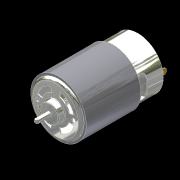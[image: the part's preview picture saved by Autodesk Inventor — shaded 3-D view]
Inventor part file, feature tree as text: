
AUTODESK INVENTOR PART (.ipt)
format: ipt  version: 2012 (Build 160160000, 160)  size: 304,640 bytes
history: native  units: mm (DEFAULTED — no unit token found)
features: sketch x15, extrude x13, fillet x3, plane x3, hole x2, mirror x2, pattern_circular x2, shell x1, chamfer x1
ambient origin geometry x8: Origin, YZ Plane, XZ Plane, XY Plane, X Axis, Y Axis, Z Axis, Center Point
bodies: Solid1 (feature_tree)
feature tree (42):
  extrude  "Extrusion1"  Depth=57.0mm TaperAngle=0.0deg
  fillet  "Fillet1"  Radius=2.0mm
  shell  "Shell1"  Thickness=0.62mm
  extrude  "Extrusion2"  Depth=4.5mm TaperAngle=0.0deg
  fillet  "Fillet2"  Radius=0.5mm
  extrude  "Extrusion3"  Depth=10.0mm TaperAngle=0.0deg
  fillet  "Fillet3"  Radius=1.6mm
  hole  "Hole1"  [1 undecoded]
  mirror  "Mirror1"
  extrude  "Extrusion4"  Depth=13.0mm
  pattern_circular  "Circular Pattern1"  Count=4 Angle=360.0deg
  plane  "Work Plane1"
  extrude  "Extrusion5"  Depth=0.62mm TaperAngle=0.0deg
  extrude  "Extrusion6"  Depth=0.62mm TaperAngle=0.0deg
  extrude  "Extrusion7"  Depth=3.0mm TaperAngle=0.0deg
  extrude  "Extrusion8"  Depth=0.8mm TaperAngle=0.0deg
  extrude  "Extrusion9"  Depth=1.0mm TaperAngle=0.0deg
  extrude  "Extrusion10"  Depth=3.15mm
  pattern_circular  "Circular Pattern2"  [2 undecoded]
  extrude  "Extrusion11"  Depth=1.0mm TaperAngle=0.0deg
  chamfer  "Chamfer1"  Distance=40.0mm Angle=360.0deg
  hole  "Hole2"  [1 undecoded]
  mirror  "Mirror2"
  plane  "Work Plane2"
  extrude  "Extrusion12"  Depth=3.8mm
  plane  "Work Plane3"
  extrude  "Flux Ring"  Depth=14.0mm
  sketch  "Sketch1"  dims[d0=35.5mm d1=57.0mm d2=0.0mm d3=2.0mm d4=0.62mm]
  sketch  "Sketch2"  dims[d5=13.0mm d6=4.5mm d7=0.0mm d8=0.5mm]
  sketch  "Sketch3"  dims[d9=3.2mm d10=10.0mm d11=0.0mm d12=1.6mm]
  sketch  "Sketch4"  dims[d13=12.5mm]
  sketch  "Sketch5"  dims[d14=2.5mm d15=6.0mm d16=4.0mm d17=2.0mm d18=14.3117mm d19=8.0mm d20=20.594885mm d21=15.0deg]
  sketch  "Sketch6"  dims[d22=15.0deg d23=13.0mm]
  sketch  "Sketch7"  dims[d24=9.5mm]
  sketch  "Sketch8"  dims[d25=10.0mm d26=0.0mm d27=40.0mm d29=360.0deg]
  sketch  "Sketch9"  dims[d30=-1.75mm d31=0.62mm d32=0.0mm]
  sketch  "Sketch10"  dims[d33=24.0mm d34=0.62mm d35=0.0mm]
  sketch  "Sketch11"  dims[d36=10.75mm d37=3.0mm d38=0.0mm]
  sketch  "Sketch12"  dims[d39=6.9mm d40=0.8mm d41=0.0mm]
  sketch  "Sketch13"  dims[d42=3.2mm d43=1.0mm d44=0.0mm]
  sketch  "Sketch14"  dims[d45=3.15mm d46=3.15mm]
  sketch  "Sketch15"  dims[d47=9.875mm d48=6.5mm d49=1.0mm d50=0.0mm d51=40.0mm d53=360.0deg d54=0.5mm d55=3.8mm d56=14.0mm d57=7.2mm d58=0.0mm d59=1.0mm d60=2.0mm d61=3.0mm d62=2.0mm d63=6.0mm d64=4.0mm d65=2.0mm d66=14.3117mm d67=1.0mm d68=20.594885mm d69=18.0mm d70=10.75mm d71=5.9mm d72=9.85mm d73=7.2mm d74=0.0mm d75=45.0deg d76=1.5mm d77=38.0mm d78=0.0mm]
note: 4 required parameter values undecoded (feature->parameter linkage not recoverable at this tier; creation-order binding heuristic only, values carry confidence <= 0.55)
